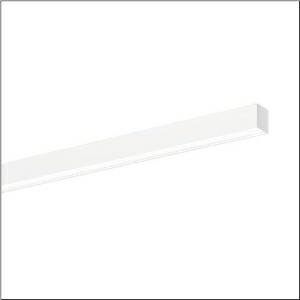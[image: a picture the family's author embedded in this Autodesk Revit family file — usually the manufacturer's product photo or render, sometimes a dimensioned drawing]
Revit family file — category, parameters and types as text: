
# Revit family: silica_r__21_51mx20tbt2w_71dc
name_source: partatom
category: Lighting Fixtures
units: mm (PartAtom-declared; Revit-internal decimal feet)

## family parameters
Cut with Voids When Loaded = No
Host = Face
Light Source = No
Part Type = Normal
Room Calculation Point = No
Round Connector Dimension = Use Diameter
Shared = No

## types (1)
- --- (1 x LED, 3000 lm, 25.6 W, 6500K)
    Apparent Load = 26 VA
    CIE Flux Codes = 48 79 96 100 100
    Color Rendering = 80
    Color Temperature = 6500K
    Default Elevation = 1800 mm
    Description = Silica® 21, office luminaire, primary optical cover: cover, of PMMA, opal, light emission: direct distribution, primary light characteristic: symmetric, installation type: surface-mounted, LED, rated luminous flux: 3.000lm, luminous efficacy: 112lm/W, light colour: 8tw, colour temperature: 2700..6500K, control gear: DALI DT8, with terminal, 3+2-pole, max. 2.5mm², mains connection: 220..240V, AC, 50/60Hz, rated input power: 26.9W, luminaire housing, of aluminium, traffic white (RAL 9016), length: 1.504mm, width: 53mm, height: 53mm, protection rating (complete): IP20, insulation class (complete): insulation class I (protective earthing), certification: CE, permissible operating ambient temperature: 0..+35°C, standard: EN 50419, packaging unit: 1 piece
    Height = 53 mm
    Lamp = 1 x LED
    Lamp Light Flux = 3000 lm
    Lamp Power = 25.6 W
    Lamp count = 1
    Length = 1504 mm
    Luminous efficacy = 117 lm/W
    Manufacturer = Siteco
    ModVariant = No
    Model = 51MX20TBT2W
    Mounting Place = Ceiling
    Mounting Type = Surface mounted
    Number of Poles = 1
    OnlyDefault = Yes
    Power Factor = 1
    Product Name = Silica® 21
    Product group = office luminaire | ceiling mounted
    ProductGroupID = 302
    Protection Class = Protection class I
    Protection Degree = IP 20
    RLX_Detail_Level = 1
    RLX_Emergency_Light_Flux = 0 lm
    RLX_Emergency_Type = 0
    RLX_Emergency_Type_DB = No
    RlxData = <blob elided: 20609 chars, md5=d50cf9e7>
    Socket = socket
    Standby Power = 0 W
    System Light Flux = 3000 lm
    System Power = 26 W
    Type Comments = individual setting
    Type Image = l_1335877.jpg
    URL = http://relux.com
    VarID = @adj_139704
    Voltage = 0 V
    Weight = 0.00 kg
    Width = 53 mm

## geometry (parser evidence)
native form markers: Blend x4, Sweep x9
no freeform markers — native parametric forms only
